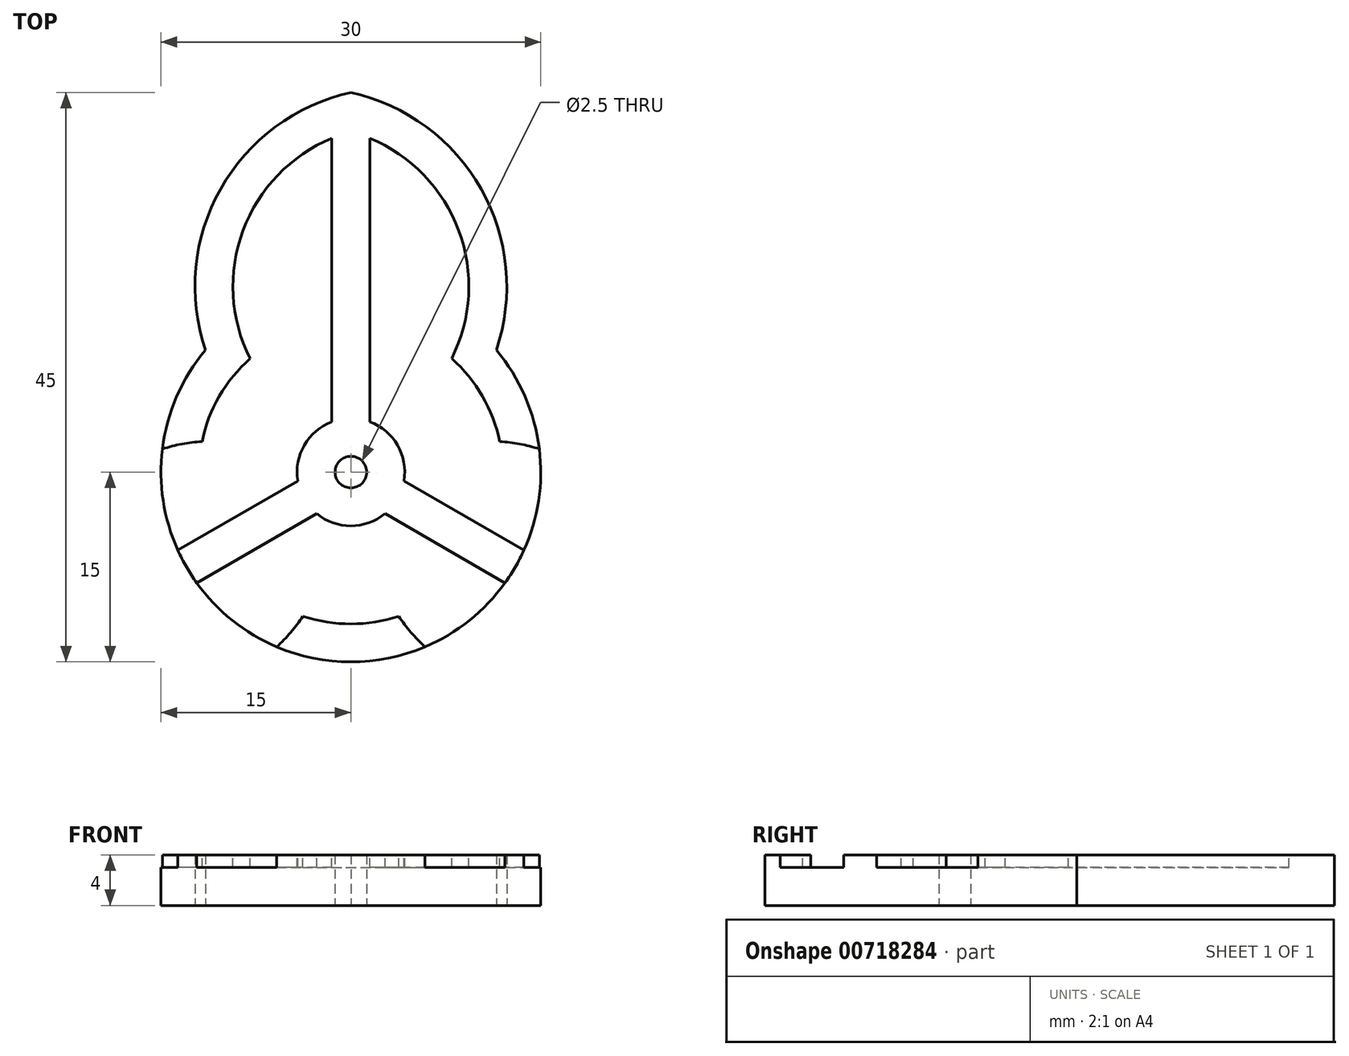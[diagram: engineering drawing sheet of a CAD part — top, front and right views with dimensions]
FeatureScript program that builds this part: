
annotation { "Feature Type Name" : "Feature", "Feature Type Description" : "" }
export const myFeature = defineFeature(function(context is Context, id is Id, definition is map)
    precondition{}
    {
        {
            var Q0;
            Q0=qCreatedBy(makeId("Top.planeOp"),FACE);
            var sketch = newSketch(context, id + "F0", { "sketchPlane" : qUnion([Q0])});
            skCircle(sketch, "E0", {"center": v(0, 0) * mm, "radius": 15 * mm});
            skLineSegment(sketch, "E1", {"start": v(0, 0) * mm, "end": v(0, 15) * mm, "construction": true});
            skLineSegment(sketch, "E2", {"start": v(0, 0) * mm, "end": v(11.5, 9.64) * mm, "construction": true});
            skCircle(sketch, "E3", {"center": v(0, 0) * mm, "radius": 30 * mm, "construction": true});
            skLineSegment(sketch, "E4", {"start": v(0, 0) * mm, "end": v(7.76, 28.98) * mm, "construction": true});
            skCircle(sketch, "E5", {"center": v(0, 0) * mm, "radius": 1.25 * mm});
            skLineSegment(sketch, "E6", {"start": v(0, 15) * mm, "end": v(0, 30) * mm});
            skArc(sketch, "E7", {"start": v(11.5, 9.64) * mm, "mid": v(10.3, 22.39) * mm, "end": v(0, 30) * mm});
            skArc(sketch, "E8.MirrorCS", {"start": v(-11.5, 9.64) * mm, "mid": v(-10.3, 22.39) * mm, "end": v(0, 30) * mm});
            skArc(sketch, "E9.1.0", {"start": v(-2.6, -14.77) * mm, "mid": v(-14.24, -20.1) * mm, "end": v(-25.98, -15) * mm});
            skArc(sketch, "E9.1.1", {"start": v(-14.1, 5.13) * mm, "mid": v(-24.53, -2.28) * mm, "end": v(-25.98, -15) * mm});
            skArc(sketch, "E9.2.0", {"start": v(14.1, 5.13) * mm, "mid": v(24.53, -2.28) * mm, "end": v(25.98, -15) * mm});
            skArc(sketch, "E9.2.1", {"start": v(2.6, -14.77) * mm, "mid": v(14.24, -20.1) * mm, "end": v(25.98, -15) * mm});
            skSolve(sketch);
        }
        {
            var Q0;
            {var subQ0=sQuery(id+"F0.wireOp",EDGE,"E9.1.0");Q0=makeQuery(id+"F0.imprint","IMPRINT",FACE,{"disambiguationData":[TD([[makeQuery(id+"F0.imprint","IMPRINT",EDGE,{"derivedFrom":subQ0}),-1.0]])]});}
            var Q1;
            Q1=makeQuery(id+"F0.imprint","IMPRINT",FACE,{"disambiguationData":[TD([[makeQuery(id+"F0.imprint","IMPRINT",EDGE,{"derivedFrom":sQuery(id+"F0.wireOp",EDGE,"E5")}),-1.0]])]});
            var Q2;
            {var subQ0=sQuery(id+"F0.wireOp",EDGE,"E6");Q2=makeQuery(id+"F0.imprint","IMPRINT",FACE,{"disambiguationData":[TD([[makeQuery(id+"F0.imprint","IMPRINT",EDGE,{"derivedFrom":subQ0}),1.0]])]});}
            var Q3;
            {var subQ0=sQuery(id+"F0.wireOp",EDGE,"E9.2.0");Q3=makeQuery(id+"F0.imprint","IMPRINT",FACE,{"disambiguationData":[TD([[makeQuery(id+"F0.imprint","IMPRINT",EDGE,{"derivedFrom":subQ0}),-1.0]])]});}
            var Q4;
            {var subQ0=sQuery(id+"F0.wireOp",EDGE,"E6");Q4=makeQuery(id+"F0.imprint","IMPRINT",FACE,{"disambiguationData":[TD([[makeQuery(id+"F0.imprint","IMPRINT",EDGE,{"derivedFrom":subQ0}),-1.0]])]});}
            extrude(context, id + "F1", {"entities" : qUnion([Q0, Q1, Q2, Q3, Q4]), "depth" : 4 * mm, "offsetDistance" : 25 * mm});
        }
        {
            var Q0;
            Q0=makeQuery(id+"F1.opExtrude","CAP_FACE",FACE,{"disambiguationData":[OSD([sQuery(id+"F0.wireOp",EDGE,"E0"),sQuery(id+"F0.wireOp",EDGE,"E5"),sQuery(id+"F0.wireOp",EDGE,"E7"),sQuery(id+"F0.wireOp",EDGE,"E8.MirrorCS"),sQuery(id+"F0.wireOp",EDGE,"E9.1.0"),sQuery(id+"F0.wireOp",EDGE,"E9.1.1"),sQuery(id+"F0.wireOp",EDGE,"E9.2.0"),sQuery(id+"F0.wireOp",EDGE,"E9.2.1")])],"isStart":false});
            var sketch = newSketch(context, id + "F2", { "sketchPlane" : qUnion([Q0])});
            skCircle(sketch, "E10.0", {"center": v(0, 0) * mm, "radius": 4.25 * mm});
            skArc(sketch, "E11.0", {"start": v(-7.97, 8.97) * mm, "mid": v(-10.4, 6) * mm, "end": v(-11.75, 2.41) * mm});
            skArc(sketch, "E11.1", {"start": v(-11.75, 2.41) * mm, "mid": v(-21.28, -2.79) * mm, "end": v(-23.3, -13.46) * mm});
            skArc(sketch, "E11.2", {"start": v(-7.97, 8.97) * mm, "mid": v(-8.22, 19.83) * mm, "end": v(0, 26.91) * mm});
            skArc(sketch, "E11.3", {"start": v(-3.79, -11.39) * mm, "mid": v(-13.06, -17.04) * mm, "end": v(-23.3, -13.46) * mm});
            skArc(sketch, "E11.4", {"start": v(-3.79, -11.39) * mm, "mid": v(0, -12) * mm, "end": v(3.79, -11.39) * mm});
            skArc(sketch, "E11.5", {"start": v(7.97, 8.97) * mm, "mid": v(8.22, 19.83) * mm, "end": v(0, 26.91) * mm});
            skArc(sketch, "E11.6", {"start": v(11.75, 2.41) * mm, "mid": v(10.4, 6) * mm, "end": v(7.97, 8.97) * mm});
            skArc(sketch, "E11.7", {"start": v(11.75, 2.41) * mm, "mid": v(21.28, -2.79) * mm, "end": v(23.3, -13.46) * mm});
            skArc(sketch, "E11.8", {"start": v(3.79, -11.39) * mm, "mid": v(13.06, -17.04) * mm, "end": v(23.3, -13.46) * mm});
            skLineSegment(sketch, "E12", {"start": v(0, 0) * mm, "end": v(0, 26.91) * mm, "construction": true});
            skLineSegment(sketch, "E13", {"start": v(1.5, 3.98) * mm, "end": v(1.5, 26.4) * mm});
            skLineSegment(sketch, "E14.MirrorCS", {"start": v(-1.5, 3.98) * mm, "end": v(-1.5, 26.4) * mm});
            skLineSegment(sketch, "E15.1.0", {"start": v(-2.7, -3.29) * mm, "end": v(-22.1, -14.5) * mm});
            skLineSegment(sketch, "E15.1.1", {"start": v(-4.2, -0.69) * mm, "end": v(-23.6, -11.9) * mm});
            skLineSegment(sketch, "E15.2.0", {"start": v(4.2, -0.69) * mm, "end": v(23.6, -11.9) * mm});
            skLineSegment(sketch, "E15.2.1", {"start": v(2.7, -3.29) * mm, "end": v(22.1, -14.5) * mm});
            skSolve(sketch);
        }
        {
            var Q0;
            {var subQ1=sQuery(id+"F2.wireOp",EDGE,"E11.0");Q0=makeQuery(id+"F2.imprint","IMPRINT",FACE,{"disambiguationData":[TD([[makeQuery(id+"F2.imprint","IMPRINT",EDGE,{"derivedFrom":subQ1}),1.0]])]});}
            var Q1;
            {var subQ1=sQuery(id+"F2.wireOp",EDGE,"E11.6");Q1=makeQuery(id+"F2.imprint","IMPRINT",FACE,{"disambiguationData":[TD([[makeQuery(id+"F2.imprint","IMPRINT",EDGE,{"derivedFrom":subQ1}),1.0]])]});}
            var Q2;
            {var subQ1=sQuery(id+"F2.wireOp",EDGE,"E11.4");Q2=makeQuery(id+"F2.imprint","IMPRINT",FACE,{"disambiguationData":[TD([[makeQuery(id+"F2.imprint","IMPRINT",EDGE,{"derivedFrom":subQ1}),1.0]])]});}
            extrude(context, id + "F3", {"entities" : qUnion([Q0, Q1, Q2]), "operationType" : NewBodyOperationType.REMOVE, "oppositeDirection" : true, "depth" : 1 * mm, "offsetDistance" : 25 * mm});
        }
    });
